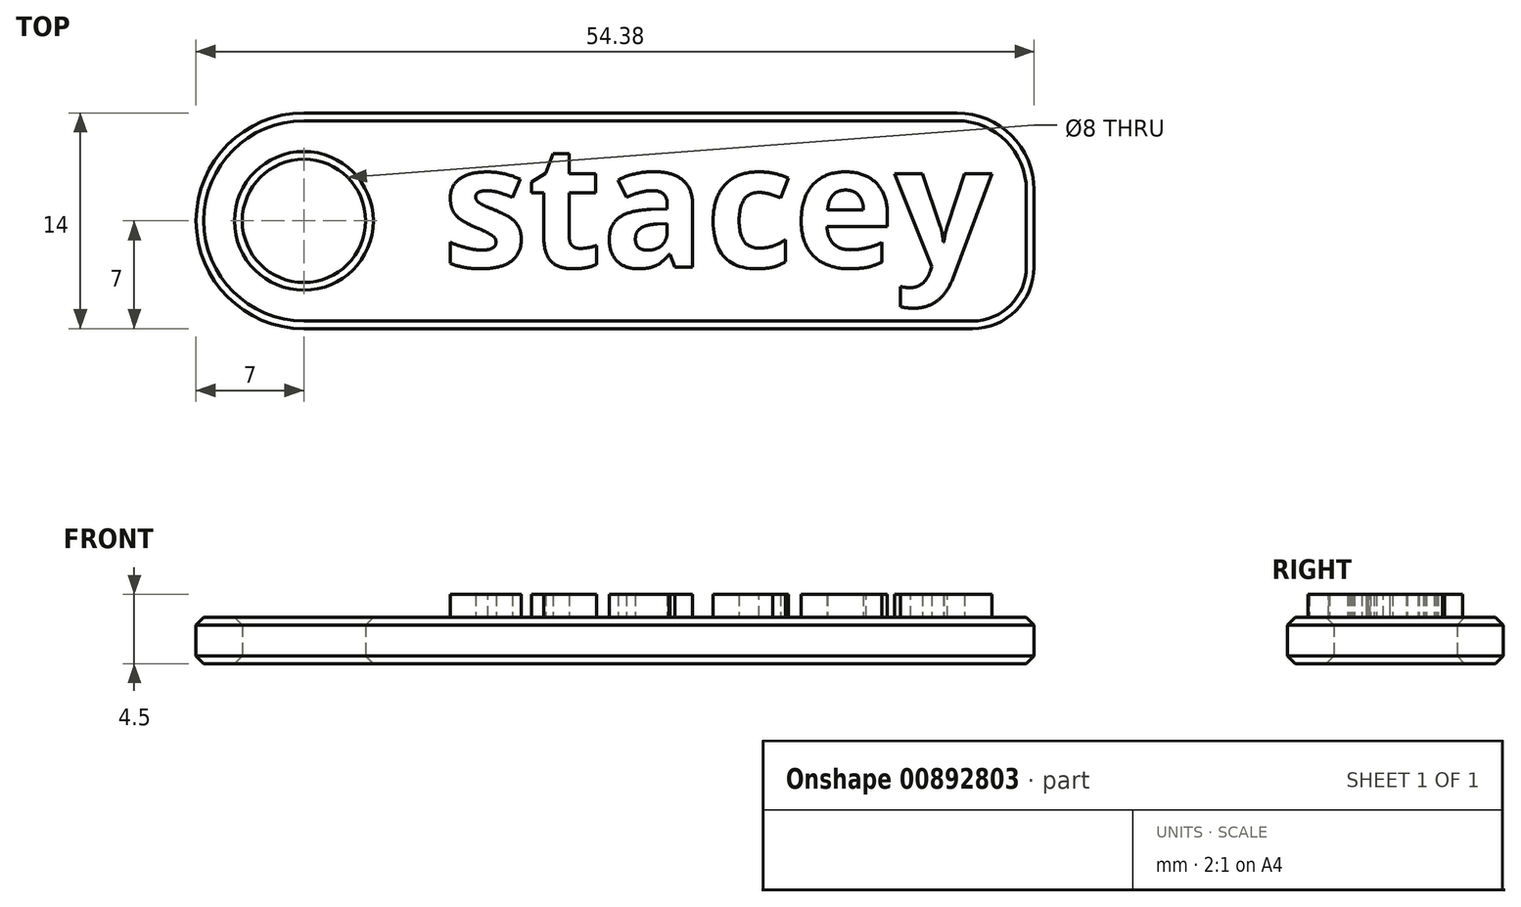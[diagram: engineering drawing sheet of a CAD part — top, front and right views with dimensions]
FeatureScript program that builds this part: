
annotation { "Feature Type Name" : "Feature", "Feature Type Description" : "" }
export const myFeature = defineFeature(function(context is Context, id is Id, definition is map)
    precondition{}
    {
        {
            var Q0;
            Q0=qCreatedBy(makeId("Top.planeOp"),FACE);
            var sketch = newSketch(context, id + "F0", { "sketchPlane" : qUnion([Q0])});
            skCircle(sketch, "E0", {"center": v(0, 0) * mm, "radius": 4 * mm});
            skCircle(sketch, "E1", {"center": v(0, 0) * mm, "radius": 7 * mm});
            skLineSegment(sketch, "E2.bottom", {"start": v(0, 7) * mm, "end": v(42.38, 7) * mm});
            skLineSegment(sketch, "E2.top", {"start": v(0, -7) * mm, "end": v(43.38, -7) * mm});
            skLineSegment(sketch, "E2.left", {"start": v(0, 7) * mm, "end": v(0, -7) * mm});
            skLineSegment(sketch, "E2.right", {"start": v(47.38, 2) * mm, "end": v(47.38, -3) * mm});
            skPoint(sketch, "E3.visualSharp", {"position": v(47.38, 7) * mm});
            skArc(sketch, "E3.filletArc", {"start": v(47.38, 2) * mm, "mid": v(45.91, 5.54) * mm, "end": v(42.38, 7) * mm});
            skPoint(sketch, "E4.visualSharp", {"position": v(47.38, -7) * mm});
            skArc(sketch, "E4.filletArc", {"start": v(43.38, -7) * mm, "mid": v(46.2, -5.83) * mm, "end": v(47.38, -3) * mm});
            skText(sketch, "E5", { "text": "stacey", "fontName": "OpenSans-Bold.ttf"});
            const initialGuessF0  = {"E5": [0.009, -0.003, 1, 0, 0.008]};
            skSetInitialGuess(sketch, initialGuessF0);
            skSolve(sketch);
        }
        {
            var Q0;
            Q0=makeQuery(id+"F0.imprint","IMPRINT",FACE,{"disambiguationData":[TD([[makeQuery(id+"F0.imprint","IMPRINT",EDGE,{"derivedFrom":sQuery(id+"F0.wireOp",EDGE,"E5.sketch_text.stroke-357")}),-1.0]])]});
            var Q1;
            Q1=makeQuery(id+"F0.imprint","IMPRINT",FACE,{"disambiguationData":[TD([[makeQuery(id+"F0.imprint","IMPRINT",EDGE,{"derivedFrom":sQuery(id+"F0.wireOp",EDGE,"E5.sketch_text.stroke-375")}),1.0]])]});
            var Q2;
            Q2=makeQuery(id+"F0.imprint","IMPRINT",FACE,{"disambiguationData":[TD([[makeQuery(id+"F0.imprint","IMPRINT",EDGE,{"derivedFrom":sQuery(id+"F0.wireOp",EDGE,"E5.sketch_text.stroke-382")}),-1.0]])]});
            var Q3;
            Q3=makeQuery(id+"F0.imprint","IMPRINT",FACE,{"disambiguationData":[TD([[makeQuery(id+"F0.imprint","IMPRINT",EDGE,{"derivedFrom":sQuery(id+"F0.wireOp",EDGE,"E5.sketch_text.stroke-410")}),-1.0]])]});
            var Q4;
            Q4=makeQuery(id+"F0.imprint","IMPRINT",FACE,{"disambiguationData":[TD([[makeQuery(id+"F0.imprint","IMPRINT",EDGE,{"derivedFrom":sQuery(id+"F0.wireOp",EDGE,"E5.sketch_text.stroke-428")}),1.0]])]});
            var Q5;
            Q5=makeQuery(id+"F0.imprint","IMPRINT",FACE,{"disambiguationData":[TD([[makeQuery(id+"F0.imprint","IMPRINT",EDGE,{"derivedFrom":sQuery(id+"F0.wireOp",EDGE,"E5.sketch_text.stroke-329")}),-1.0]])]});
            var Q6;
            Q6=makeQuery(id+"F0.imprint","IMPRINT",FACE,{"disambiguationData":[TD([[makeQuery(id+"F0.imprint","IMPRINT",EDGE,{"derivedFrom":sQuery(id+"F0.wireOp",EDGE,"E5.sketch_text.stroke-304")}),-1.0]])]});
            var Q7;
            Q7=makeQuery(id+"F0.imprint","IMPRINT",FACE,{"disambiguationData":[TD([[makeQuery(id+"F0.imprint","IMPRINT",EDGE,{"derivedFrom":sQuery(id+"F0.wireOp",EDGE,"E5.sketch_text.stroke-322")}),1.0]])]});
            var Q8;
            Q8=makeQuery(id+"F0.imprint","IMPRINT",FACE,{"disambiguationData":[TD([[makeQuery(id+"F0.imprint","IMPRINT",EDGE,{"derivedFrom":sQuery(id+"F0.wireOp",EDGE,"E5.sketch_text.stroke-269")}),1.0]])]});
            var Q9;
            Q9=makeQuery(id+"F0.imprint","IMPRINT",FACE,{"disambiguationData":[TD([[makeQuery(id+"F0.imprint","IMPRINT",EDGE,{"derivedFrom":sQuery(id+"F0.wireOp",EDGE,"E5.sketch_text.stroke-216")}),1.0]])]});
            var Q10;
            Q10=makeQuery(id+"F0.imprint","IMPRINT",FACE,{"disambiguationData":[TD([[makeQuery(id+"F0.imprint","IMPRINT",EDGE,{"derivedFrom":sQuery(id+"F0.wireOp",EDGE,"E5.sketch_text.stroke-163")}),1.0]])]});
            var Q11;
            Q11=makeQuery(id+"F0.imprint","IMPRINT",FACE,{"disambiguationData":[TD([[makeQuery(id+"F0.imprint","IMPRINT",EDGE,{"derivedFrom":sQuery(id+"F0.wireOp",EDGE,"E5.sketch_text.stroke-110")}),1.0]])]});
            var Q12;
            Q12=makeQuery(id+"F0.imprint","IMPRINT",FACE,{"disambiguationData":[TD([[makeQuery(id+"F0.imprint","IMPRINT",EDGE,{"derivedFrom":sQuery(id+"F0.wireOp",EDGE,"E5.sketch_text.stroke-18")}),1.0]])]});
            var Q13;
            Q13=makeQuery(id+"F0.imprint","IMPRINT",FACE,{"disambiguationData":[TD([[makeQuery(id+"F0.imprint","IMPRINT",EDGE,{"derivedFrom":sQuery(id+"F0.wireOp",EDGE,"E5.sketch_text.stroke-0")}),-1.0]])]});
            var Q14;
            Q14=makeQuery(id+"F0.imprint","IMPRINT",FACE,{"disambiguationData":[TD([[makeQuery(id+"F0.imprint","IMPRINT",EDGE,{"derivedFrom":sQuery(id+"F0.wireOp",EDGE,"E5.sketch_text.stroke-25")}),-1.0]])]});
            var Q15;
            Q15=makeQuery(id+"F0.imprint","IMPRINT",FACE,{"disambiguationData":[TD([[makeQuery(id+"F0.imprint","IMPRINT",EDGE,{"derivedFrom":sQuery(id+"F0.wireOp",EDGE,"E5.sketch_text.stroke-42")}),-1.0]])]});
            var Q16;
            Q16=makeQuery(id+"F0.imprint","IMPRINT",FACE,{"disambiguationData":[TD([[makeQuery(id+"F0.imprint","IMPRINT",EDGE,{"derivedFrom":sQuery(id+"F0.wireOp",EDGE,"E5.sketch_text.stroke-59")}),-1.0]])]});
            var Q17;
            Q17=makeQuery(id+"F0.imprint","IMPRINT",FACE,{"disambiguationData":[TD([[makeQuery(id+"F0.imprint","IMPRINT",EDGE,{"derivedFrom":sQuery(id+"F0.wireOp",EDGE,"E5.sketch_text.stroke-64")}),-1.0]])]});
            var Q18;
            Q18=makeQuery(id+"F0.imprint","IMPRINT",FACE,{"disambiguationData":[TD([[makeQuery(id+"F0.imprint","IMPRINT",EDGE,{"derivedFrom":sQuery(id+"F0.wireOp",EDGE,"E5.sketch_text.stroke-92")}),-1.0]])]});
            var Q19;
            Q19=makeQuery(id+"F0.imprint","IMPRINT",FACE,{"disambiguationData":[TD([[makeQuery(id+"F0.imprint","IMPRINT",EDGE,{"derivedFrom":sQuery(id+"F0.wireOp",EDGE,"E5.sketch_text.stroke-117")}),-1.0]])]});
            var Q20;
            Q20=makeQuery(id+"F0.imprint","IMPRINT",FACE,{"disambiguationData":[TD([[makeQuery(id+"F0.imprint","IMPRINT",EDGE,{"derivedFrom":sQuery(id+"F0.wireOp",EDGE,"E5.sketch_text.stroke-145")}),-1.0]])]});
            var Q21;
            Q21=makeQuery(id+"F0.imprint","IMPRINT",FACE,{"disambiguationData":[TD([[makeQuery(id+"F0.imprint","IMPRINT",EDGE,{"derivedFrom":sQuery(id+"F0.wireOp",EDGE,"E5.sketch_text.stroke-170")}),-1.0]])]});
            var Q22;
            Q22=makeQuery(id+"F0.imprint","IMPRINT",FACE,{"disambiguationData":[TD([[makeQuery(id+"F0.imprint","IMPRINT",EDGE,{"derivedFrom":sQuery(id+"F0.wireOp",EDGE,"E5.sketch_text.stroke-198")}),-1.0]])]});
            var Q23;
            Q23=makeQuery(id+"F0.imprint","IMPRINT",FACE,{"disambiguationData":[TD([[makeQuery(id+"F0.imprint","IMPRINT",EDGE,{"derivedFrom":sQuery(id+"F0.wireOp",EDGE,"E5.sketch_text.stroke-223")}),-1.0]])]});
            var Q24;
            Q24=makeQuery(id+"F0.imprint","IMPRINT",FACE,{"disambiguationData":[TD([[makeQuery(id+"F0.imprint","IMPRINT",EDGE,{"derivedFrom":sQuery(id+"F0.wireOp",EDGE,"E5.sketch_text.stroke-251")}),-1.0]])]});
            var Q25;
            Q25=makeQuery(id+"F0.imprint","IMPRINT",FACE,{"disambiguationData":[TD([[makeQuery(id+"F0.imprint","IMPRINT",EDGE,{"derivedFrom":sQuery(id+"F0.wireOp",EDGE,"E5.sketch_text.stroke-276")}),-1.0]])]});
            var Q26;
            {var subQ1=sQuery(id+"F0.wireOp",EDGE,"E2.bottom");Q26=makeQuery(id+"F0.imprint","IMPRINT",FACE,{"disambiguationData":[TD([[makeQuery(id+"F0.imprint","IMPRINT",EDGE,{"derivedFrom":subQ1}),-1.0]])]});}
            var Q27;
            {var subQ0=sQuery(id+"F0.wireOp",EDGE,"E2.left");var subQ1=sQuery(id+"F0.wireOp",EDGE,"E0");var subQ2=makeQuery(id+"F0.imprint","INTERSECT",VERTEX,{"disambiguationData":[OD(0.0)],"derivedFrom":[subQ1,subQ0]});Q27=makeQuery(id+"F0.imprint","IMPRINT",FACE,{"disambiguationData":[TD([[makeQuery(id+"F0.imprint","IMPRINT",EDGE,{"disambiguationData":[TD([[subQ2,-1.0]])],"derivedFrom":subQ1}),-1.0]])]});}
            var Q28;
            {var subQ0=sQuery(id+"F0.wireOp",EDGE,"E2.left");var subQ1=sQuery(id+"F0.wireOp",EDGE,"E0");var subQ2=makeQuery(id+"F0.imprint","INTERSECT",VERTEX,{"disambiguationData":[OD(0.0)],"derivedFrom":[subQ1,subQ0]});Q28=makeQuery(id+"F0.imprint","IMPRINT",FACE,{"disambiguationData":[TD([[makeQuery(id+"F0.imprint","IMPRINT",EDGE,{"disambiguationData":[TD([[subQ2,1.0]])],"derivedFrom":subQ1}),-1.0]])]});}
            var Q29;
            Q29=makeQuery(id+"F0.imprint","IMPRINT",FACE,{"disambiguationData":[TD([[makeQuery(id+"F0.imprint","IMPRINT",EDGE,{"derivedFrom":sQuery(id+"F0.wireOp",EDGE,"E5.sketch_text.stroke-20")}),-1.0]])]});
            var Q30;
            Q30=makeQuery(id+"F0.imprint","IMPRINT",FACE,{"disambiguationData":[TD([[makeQuery(id+"F0.imprint","IMPRINT",EDGE,{"derivedFrom":sQuery(id+"F0.wireOp",EDGE,"E5.sketch_text.stroke-15")}),-1.0]])]});
            var Q31;
            Q31=makeQuery(id+"F0.imprint","IMPRINT",FACE,{"disambiguationData":[TD([[makeQuery(id+"F0.imprint","IMPRINT",EDGE,{"derivedFrom":sQuery(id+"F0.wireOp",EDGE,"E5.sketch_text.stroke-87")}),1.0]])]});
            var Q32;
            Q32=makeQuery(id+"F0.imprint","IMPRINT",FACE,{"disambiguationData":[TD([[makeQuery(id+"F0.imprint","IMPRINT",EDGE,{"derivedFrom":sQuery(id+"F0.wireOp",EDGE,"E5.sketch_text.stroke-96")}),-1.0]])]});
            var Q33;
            Q33=makeQuery(id+"F0.imprint","IMPRINT",FACE,{"disambiguationData":[TD([[makeQuery(id+"F0.imprint","IMPRINT",EDGE,{"derivedFrom":sQuery(id+"F0.wireOp",EDGE,"E5.sketch_text.stroke-49")}),1.0]])]});
            var Q34;
            Q34=makeQuery(id+"F0.imprint","IMPRINT",FACE,{"disambiguationData":[TD([[makeQuery(id+"F0.imprint","IMPRINT",EDGE,{"derivedFrom":sQuery(id+"F0.wireOp",EDGE,"E5.sketch_text.stroke-127")}),1.0]])]});
            var Q35;
            Q35=makeQuery(id+"F0.imprint","IMPRINT",FACE,{"disambiguationData":[TD([[makeQuery(id+"F0.imprint","IMPRINT",EDGE,{"derivedFrom":sQuery(id+"F0.wireOp",EDGE,"E5.sketch_text.stroke-65")}),1.0]])]});
            var Q36;
            Q36=makeQuery(id+"F0.imprint","IMPRINT",FACE,{"disambiguationData":[TD([[makeQuery(id+"F0.imprint","IMPRINT",EDGE,{"derivedFrom":sQuery(id+"F0.wireOp",EDGE,"E5.sketch_text.stroke-74")}),-1.0]])]});
            var Q37;
            Q37=makeQuery(id+"F0.imprint","IMPRINT",FACE,{"disambiguationData":[TD([[makeQuery(id+"F0.imprint","IMPRINT",EDGE,{"derivedFrom":sQuery(id+"F0.wireOp",EDGE,"E5.sketch_text.stroke-131")}),1.0]])]});
            var Q38;
            Q38=makeQuery(id+"F0.imprint","IMPRINT",FACE,{"disambiguationData":[TD([[makeQuery(id+"F0.imprint","IMPRINT",EDGE,{"derivedFrom":sQuery(id+"F0.wireOp",EDGE,"E5.sketch_text.stroke-87")}),-1.0]])]});
            var Q39;
            Q39=makeQuery(id+"F0.imprint","IMPRINT",FACE,{"disambiguationData":[TD([[makeQuery(id+"F0.imprint","IMPRINT",EDGE,{"derivedFrom":sQuery(id+"F0.wireOp",EDGE,"E5.sketch_text.stroke-35")}),1.0]])]});
            var Q40;
            Q40=makeQuery(id+"F0.imprint","IMPRINT",FACE,{"disambiguationData":[TD([[makeQuery(id+"F0.imprint","IMPRINT",EDGE,{"derivedFrom":sQuery(id+"F0.wireOp",EDGE,"E5.sketch_text.stroke-73")}),1.0]])]});
            var Q41;
            Q41=makeQuery(id+"F0.imprint","IMPRINT",FACE,{"disambiguationData":[TD([[makeQuery(id+"F0.imprint","IMPRINT",EDGE,{"derivedFrom":sQuery(id+"F0.wireOp",EDGE,"E5.sketch_text.stroke-82")}),1.0]])]});
            extrude(context, id + "F1", {"entities" : qUnion([Q0, Q1, Q2, Q3, Q4, Q5, Q6, Q7, Q8, Q9, Q10, Q11, Q12, Q13, Q14, Q15, Q16, Q17, Q18, Q19, Q20, Q21, Q22, Q23, Q24, Q25, Q26, Q27, Q28, Q29, Q30, Q31, Q32, Q33, Q34, Q35, Q36, Q37, Q38, Q39, Q40, Q41]), "depth" : 3 * mm, "offsetDistance" : 25 * mm});
        }
        {
            var Q0;
            Q0=makeQuery(id+"F0.imprint","IMPRINT",FACE,{"disambiguationData":[TD([[makeQuery(id+"F0.imprint","IMPRINT",EDGE,{"derivedFrom":sQuery(id+"F0.wireOp",EDGE,"E5.sketch_text.stroke-0")}),-1.0]])]});
            var Q1;
            Q1=makeQuery(id+"F0.imprint","IMPRINT",FACE,{"disambiguationData":[TD([[makeQuery(id+"F0.imprint","IMPRINT",EDGE,{"derivedFrom":sQuery(id+"F0.wireOp",EDGE,"E5.sketch_text.stroke-26")}),-1.0]])]});
            var Q2;
            Q2=makeQuery(id+"F0.imprint","IMPRINT",FACE,{"disambiguationData":[TD([[makeQuery(id+"F0.imprint","IMPRINT",EDGE,{"derivedFrom":sQuery(id+"F0.wireOp",EDGE,"E5.sketch_text.stroke-51")}),-1.0]])]});
            var Q3;
            Q3=makeQuery(id+"F0.imprint","IMPRINT",FACE,{"disambiguationData":[TD([[makeQuery(id+"F0.imprint","IMPRINT",EDGE,{"derivedFrom":sQuery(id+"F0.wireOp",EDGE,"E5.sketch_text.stroke-74")}),-1.0]])]});
            var Q4;
            Q4=makeQuery(id+"F0.imprint","IMPRINT",FACE,{"disambiguationData":[TD([[makeQuery(id+"F0.imprint","IMPRINT",EDGE,{"derivedFrom":sQuery(id+"F0.wireOp",EDGE,"E5.sketch_text.stroke-92")}),-1.0]])]});
            var Q5;
            Q5=makeQuery(id+"F0.imprint","IMPRINT",FACE,{"disambiguationData":[TD([[makeQuery(id+"F0.imprint","IMPRINT",EDGE,{"derivedFrom":sQuery(id+"F0.wireOp",EDGE,"E5.sketch_text.stroke-87")}),-1.0]])]});
            var Q6;
            Q6=makeQuery(id+"F0.imprint","IMPRINT",FACE,{"disambiguationData":[TD([[makeQuery(id+"F0.imprint","IMPRINT",EDGE,{"derivedFrom":sQuery(id+"F0.wireOp",EDGE,"E5.sketch_text.stroke-96")}),-1.0]])]});
            var Q7;
            Q7=makeQuery(id+"F0.imprint","IMPRINT",FACE,{"disambiguationData":[TD([[makeQuery(id+"F0.imprint","IMPRINT",EDGE,{"derivedFrom":sQuery(id+"F0.wireOp",EDGE,"E5.sketch_text.stroke-113")}),-1.0]])]});
            extrude(context, id + "F2", {"entities" : qUnion([Q0, Q1, Q2, Q3, Q4, Q5, Q6, Q7]), "operationType" : NewBodyOperationType.ADD, "depth" : 4.5 * mm, "offsetDistance" : 25 * mm});
        }
        {
            var Q0;
            Q0=makeQuery(id+"F1.opExtrude","CAP_EDGE",EDGE,{"disambiguationData":[OSD([sQuery(id+"F0.wireOp",EDGE,"E0")])],"isStart":true});
            var Q1;
            Q1=makeQuery(id+"F1.opExtrude","CAP_EDGE",EDGE,{"disambiguationData":[OSD([sQuery(id+"F0.wireOp",EDGE,"E2.right")])],"isStart":true});
            var Q2;
            Q2=makeQuery(id+"F1.opExtrude","CAP_EDGE",EDGE,{"disambiguationData":[OSD([sQuery(id+"F0.wireOp",EDGE,"E2.right")])],"isStart":false});
            var Q3;
            Q3=makeQuery(id+"F1.opExtrude","CAP_EDGE",EDGE,{"disambiguationData":[OSD([sQuery(id+"F0.wireOp",EDGE,"E0")])],"isStart":false});
            chamfer(context, id + "F3", {"entities" : qUnion([Q0, Q1, Q2, Q3]), "width" : 0.5 * mm, "tangentPropagation" : true});
        }
    });
